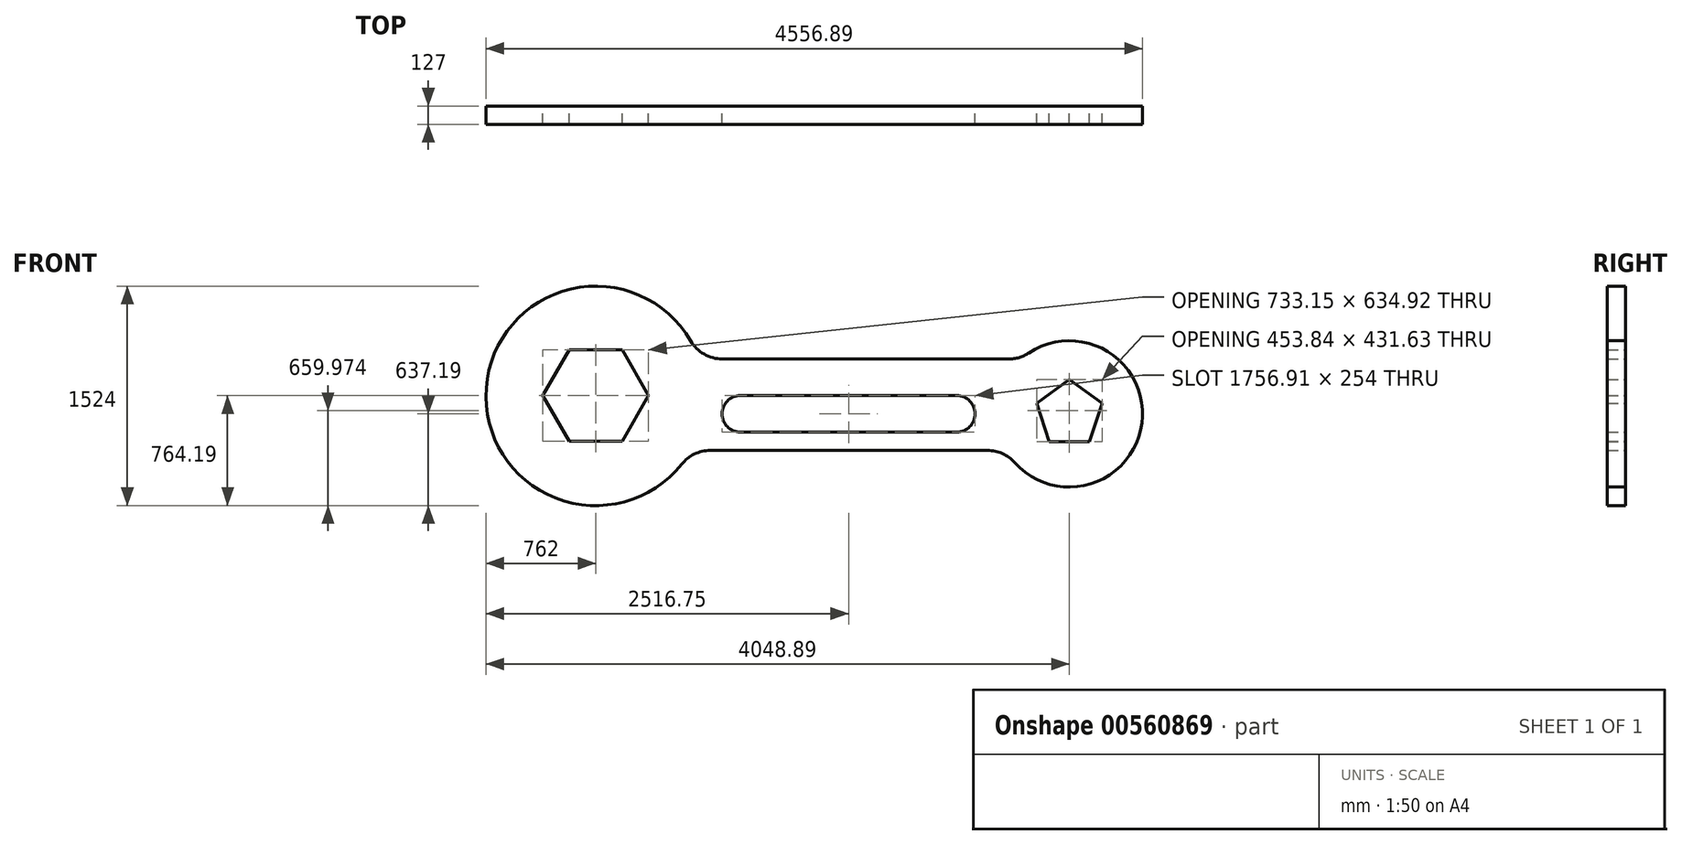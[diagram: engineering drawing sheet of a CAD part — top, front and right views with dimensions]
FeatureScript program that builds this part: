
annotation { "Feature Type Name" : "Feature", "Feature Type Description" : "" }
export const myFeature = defineFeature(function(context is Context, id is Id, definition is map)
    precondition{}
    {
        {
            var Q0;
            Q0=qCreatedBy(makeId("Front.planeOp"),FACE);
            var sketch = newSketch(context, id + "F0", { "sketchPlane" : qUnion([Q0])});
            skCircle(sketch, "E0", {"center": v(0, -2.19) * mm, "radius": 762 * mm});
            skCircle(sketch, "E1", {"center": v(3286.89, -127) * mm, "radius": 508 * mm});
            skLineSegment(sketch, "E2", {"start": v(1765.3, 0) * mm, "end": v(2506.2, 0) * mm});
            skLineSegment(sketch, "E3", {"start": v(2506.2, -254) * mm, "end": v(1003.3, -254) * mm});
            skLineSegment(sketch, "E4", {"start": v(1003.3, 0) * mm, "end": v(1765.3, 0) * mm});
            skArc(sketch, "E5", {"start": v(1003.3, 0) * mm, "mid": v(876.3, -127) * mm, "end": v(1003.3, -254) * mm});
            skArc(sketch, "E6", {"start": v(2506.2, -254) * mm, "mid": v(2633.2, -127) * mm, "end": v(2506.2, 0) * mm});
            skLineSegment(sketch, "E7", {"start": v(1765.3, -381) * mm, "end": v(794.86, -381) * mm});
            skLineSegment(sketch, "E8", {"start": v(1765.3, -381) * mm, "end": v(2718.93, -381) * mm});
            skLineSegment(sketch, "E9", {"start": v(1765.3, 254) * mm, "end": v(878.62, 254) * mm});
            skLineSegment(sketch, "E10", {"start": v(1765.3, 254) * mm, "end": v(2865.68, 254) * mm});
            skArc(sketch, "E11", {"start": v(794.86, -381) * mm, "mid": v(684.56, -406.2) * mm, "end": v(596.15, -476.8) * mm});
            skPoint(sketch, "E12.orphan", {"position": v(876.3, 0) * mm});
            skPoint(sketch, "E13.orphan", {"position": v(876.3, -254) * mm});
            skArc(sketch, "E14", {"start": v(658.96, 380.45) * mm, "mid": v(751.89, 287.87) * mm, "end": v(878.62, 254) * mm});
            skArc(sketch, "E15", {"start": v(2865.68, 254) * mm, "mid": v(2939, 264.81) * mm, "end": v(3006.08, 296.33) * mm});
            skArc(sketch, "E16", {"start": v(2908.25, -465.67) * mm, "mid": v(2822.62, -403.13) * mm, "end": v(2718.93, -381) * mm});
            skCircle(sketch, "E17.cCircle", {"center": v(0, 0) * mm, "radius": 317.46 * mm, "construction": true});
            skLineSegment(sketch, "E17.0", {"start": v(-183.29, 317.46) * mm, "end": v(183.29, 317.46) * mm});
            skLineSegment(sketch, "E17.1", {"start": v(183.29, 317.46) * mm, "end": v(366.57, 0) * mm});
            skLineSegment(sketch, "E17.2", {"start": v(366.57, 0) * mm, "end": v(183.29, -317.46) * mm});
            skLineSegment(sketch, "E17.3", {"start": v(183.29, -317.46) * mm, "end": v(-183.29, -317.46) * mm});
            skLineSegment(sketch, "E17.4", {"start": v(-183.29, -317.46) * mm, "end": v(-366.57, 0) * mm});
            skLineSegment(sketch, "E17.5", {"start": v(-366.57, 0) * mm, "end": v(-183.29, 317.46) * mm});
            skPoint(sketch, "E17.0.midPoint", {"position": v(0, 317.46) * mm});
            skPoint(sketch, "E18.0.midPoint", {"position": v(3286.89, -406.3) * mm});
            skCircle(sketch, "E19.cCircle", {"center": v(3286.89, -127) * mm, "radius": 193.03 * mm, "construction": true});
            skLineSegment(sketch, "E19.0", {"start": v(3427.13, -320.03) * mm, "end": v(3146.64, -320.03) * mm});
            skLineSegment(sketch, "E19.1", {"start": v(3146.64, -320.03) * mm, "end": v(3059.97, -53.27) * mm});
            skLineSegment(sketch, "E19.2", {"start": v(3059.97, -53.27) * mm, "end": v(3286.89, 111.6) * mm});
            skLineSegment(sketch, "E19.3", {"start": v(3286.89, 111.6) * mm, "end": v(3513.8, -53.27) * mm});
            skLineSegment(sketch, "E19.4", {"start": v(3513.8, -53.27) * mm, "end": v(3427.13, -320.03) * mm});
            skPoint(sketch, "E19.0.midPoint", {"position": v(3286.89, -320.03) * mm});
            skPoint(sketch, "E20.orphan", {"position": v(751.7, -127) * mm});
            skLineSegment(sketch, "E21.trimOffspring", {"start": v(2506.2, -127) * mm, "end": v(2633.2, -127) * mm});
            skPoint(sketch, "E22.start.orphan", {"position": v(876.3, -127) * mm});
            skPoint(sketch, "E23.orphan", {"position": v(1765.3, -127) * mm});
            skPoint(sketch, "E24.orphan", {"position": v(2778.89, -127) * mm});
            skSolve(sketch);
        }
        {
            var Q0;
            Q0 = qSketchRegion(id + "F0", true);
            extrude(context, id + "F1", {"entities" : qUnion([Q0]), "depth" : 127 * mm, "offsetDistance" : 25.4 * mm});
        }
    });
